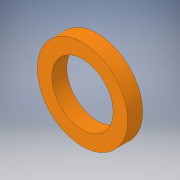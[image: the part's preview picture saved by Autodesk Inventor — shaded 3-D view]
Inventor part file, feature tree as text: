
AUTODESK INVENTOR PART (.ipt)
format: ipt  version: 2017 (Build 210142000, 142)  size: 102,400 bytes
history: native  units: in
note: dims shown in document units (in); Inventor stores cm internally (conversion verified against a paired STEP export)
features: sketch x2, extrude x1, hole x1
ambient origin geometry x8: Origin, YZ Plane, XZ Plane, XY Plane, X Axis, Y Axis, Z Axis, Center Point
bodies: Solid1 (feature_tree)
feature tree (4):
  extrude  "Extrusion1"  Depth=0.125in TaperAngle=0.0deg
  hole  "Hole1"  [1 undecoded]
  sketch  "Sketch1"  dims[d0=0.75in d1=0.125in d2=0.0in]
  sketch  "Sketch2"  dims[d3=0.51in d4=0.75in d5=0.375in d6=0.25in d7=0.5635in d8=1.0in d9=0.8108in]
note: 1 required parameter value undecoded (feature->parameter linkage not recoverable at this tier; creation-order binding heuristic only, values carry confidence <= 0.55)
